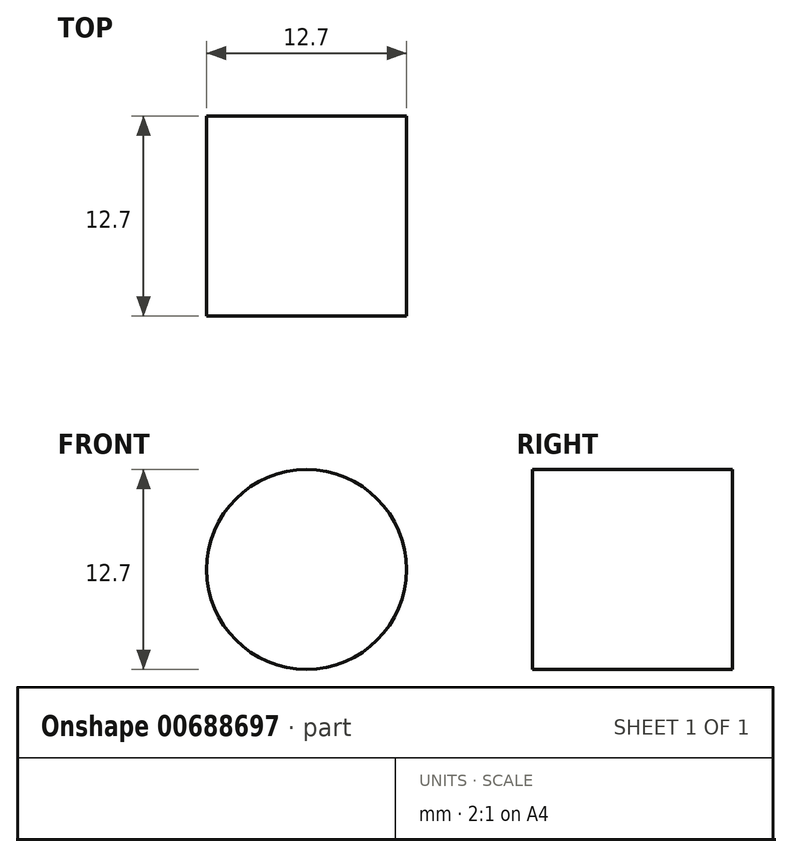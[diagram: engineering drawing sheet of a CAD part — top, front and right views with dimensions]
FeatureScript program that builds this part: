
annotation { "Feature Type Name" : "Feature", "Feature Type Description" : "" }
export const myFeature = defineFeature(function(context is Context, id is Id, definition is map)
    precondition{}
    {
        {
            var Q0;
            Q0=qCreatedBy(makeId("Front.planeOp"),FACE);
            var sketch = newSketch(context, id + "F0", { "sketchPlane" : qUnion([Q0])});
            skCircle(sketch, "E0", {"center": v(0, 0) * mm, "radius": 6.35 * mm});
            skSolve(sketch);
        }
        {
            var Q0;
            Q0 = qSketchRegion(id + "F0", true);
            extrude(context, id + "F1", {"entities" : qUnion([Q0]), "depth" : 12.7 * mm, "offsetDistance" : 25.4 * mm});
        }
    });
